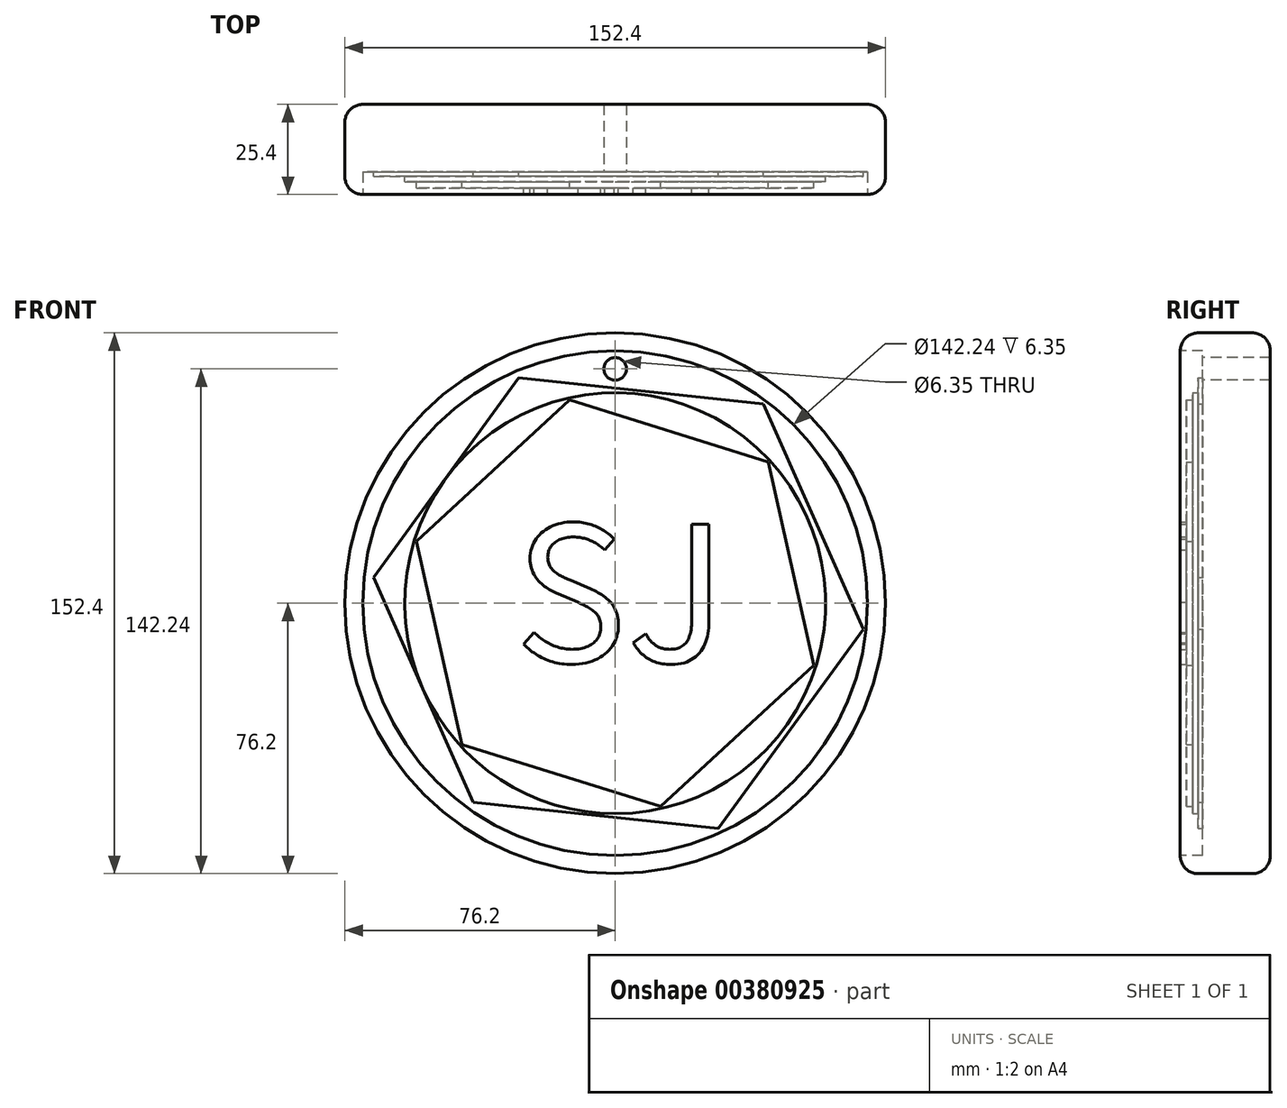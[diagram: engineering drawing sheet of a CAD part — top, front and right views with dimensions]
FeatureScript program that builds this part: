
annotation { "Feature Type Name" : "Feature", "Feature Type Description" : "" }
export const myFeature = defineFeature(function(context is Context, id is Id, definition is map)
    precondition{}
    {
        {
            var Q0;
            Q0=qCreatedBy(makeId("Front.planeOp"),FACE);
            var sketch = newSketch(context, id + "F0", { "sketchPlane" : qUnion([Q0])});
            skCircle(sketch, "E0", {"center": v(0, 0) * mm, "radius": 76.2 * mm});
            skSolve(sketch);
        }
        {
            var Q0;
            Q0 = qSketchRegion(id + "F0", true);
            extrude(context, id + "F1", {"entities" : qUnion([Q0]), "depth" : 25.4 * mm});
        }
        {
            var Q0;
            Q0=makeQuery(id+"F1.opExtrude","SWEPT_FACE",FACE,{"disambiguationData":[OSD([sQuery(id+"F0.wireOp",EDGE,"E0")])]});
            fillet(context, id + "F2", {"entities" : qUnion([Q0]), "radius" : 5.08 * mm, "tangentPropagation" : true, "allowEdgeOverflow" : false});
        }
        {
            var Q0;
            Q0=makeQuery(id+"F1.opExtrude","CAP_FACE",FACE,{"disambiguationData":[OSD([sQuery(id+"F0.wireOp",EDGE,"E0")])],"isStart":false});
            extrude(context, id + "F3", {"entities" : qUnion([Q0]), "operationType" : NewBodyOperationType.REMOVE, "oppositeDirection" : true, "depth" : 6.35 * mm});
        }
        {
            var Q0;
            Q0=makeQuery(id+"F3.boolean.opBoolean","COPY",FACE,{"derivedFrom":makeQuery(id+"F3.opExtrude","CAP_FACE",FACE,{"disambiguationData":[OSD([sQuery(id+"F0.wireOp",EDGE,"E0")])],"isStart":false})});
            var sketch = newSketch(context, id + "F4", { "sketchPlane" : qUnion([Q0])});
            skText(sketch, "E1", { "text": "SJ", "fontName": "NotoSansCJKjp-Regular.otf"});
            const initialGuessF4  = {"E1": [-0.02833, -0.01657, 1, 0, 0.0381]};
            skSetInitialGuess(sketch, initialGuessF4);
            skSolve(sketch);
        }
        {
            var Q0;
            Q0 = qSketchRegion(id + "F4", true);
            extrude(context, id + "F5", {"entities" : qUnion([Q0]), "operationType" : NewBodyOperationType.ADD, "depth" : 6.35 * mm});
        }
        {
            var Q0;
            Q0=makeQuery(id+"F3.boolean.opBoolean","COPY",FACE,{"derivedFrom":makeQuery(id+"F3.opExtrude","CAP_FACE",FACE,{"disambiguationData":[OSD([sQuery(id+"F0.wireOp",EDGE,"E0")])],"isStart":false})});
            var sketch = newSketch(context, id + "F6", { "sketchPlane" : qUnion([Q0])});
            skCircle(sketch, "E2", {"center": v(0, 66.04) * mm, "radius": 3.18 * mm});
            skSolve(sketch);
        }
        {
            var Q0;
            Q0=makeQuery(id+"F6.imprint","IMPRINT",FACE,{"disambiguationData":[TD([[makeQuery(id+"F6.imprint","IMPRINT",EDGE,{"derivedFrom":sQuery(id+"F6.wireOp",EDGE,"E2")}),1.0]])]});
            extrude(context, id + "F7", {"entities" : qUnion([Q0]), "operationType" : NewBodyOperationType.REMOVE, "oppositeDirection" : true, "depth" : 25.4 * mm});
        }
        {
            var Q0;
            Q0=makeQuery(id+"F3.boolean.opBoolean","COPY",FACE,{"derivedFrom":makeQuery(id+"F3.opExtrude","CAP_FACE",FACE,{"disambiguationData":[OSD([sQuery(id+"F0.wireOp",EDGE,"E0")])],"isStart":false})});
            var sketch = newSketch(context, id + "F8", { "sketchPlane" : qUnion([Q0])});
            skCircle(sketch, "E3.cCircle", {"center": v(0.93, 0) * mm, "radius": 60.15 * mm, "construction": true});
            skLineSegment(sketch, "E3.0", {"start": v(70, -7.34) * mm, "end": v(29.1, -63.49) * mm});
            skLineSegment(sketch, "E3.1", {"start": v(29.1, -63.49) * mm, "end": v(-39.97, -56.15) * mm});
            skLineSegment(sketch, "E3.2", {"start": v(-39.97, -56.15) * mm, "end": v(-68.14, 7.34) * mm});
            skLineSegment(sketch, "E3.3", {"start": v(-68.14, 7.34) * mm, "end": v(-27.25, 63.49) * mm});
            skLineSegment(sketch, "E3.4", {"start": v(-27.25, 63.49) * mm, "end": v(41.82, 56.15) * mm});
            skLineSegment(sketch, "E3.5", {"start": v(41.82, 56.15) * mm, "end": v(70, -7.34) * mm});
            skPoint(sketch, "E3.0.midPoint", {"position": v(49.55, -35.41) * mm});
            skSolve(sketch);
        }
        {
            var Q0;
            Q0 = qSketchRegion(id + "F8", true);
            extrude(context, id + "F9", {"entities" : qUnion([Q0]), "operationType" : NewBodyOperationType.ADD, "depth" : 1.27 * mm});
        }
        {
            var Q0;
            Q0=makeQuery(id+"F9.opExtrude","CAP_FACE",FACE,{"disambiguationData":[OSD([sQuery(id+"F8.wireOp",EDGE,"E3.0"),sQuery(id+"F8.wireOp",EDGE,"E3.1"),sQuery(id+"F8.wireOp",EDGE,"E3.2"),sQuery(id+"F8.wireOp",EDGE,"E3.3"),sQuery(id+"F8.wireOp",EDGE,"E3.4"),sQuery(id+"F8.wireOp",EDGE,"E3.5")])],"isStart":false});
            var sketch = newSketch(context, id + "F10", { "sketchPlane" : qUnion([Q0])});
            skCircle(sketch, "E4", {"center": v(0, 0) * mm, "radius": 59.3 * mm});
            skSolve(sketch);
        }
        {
            var Q0;
            Q0 = qSketchRegion(id + "F10", true);
            extrude(context, id + "F11", {"entities" : qUnion([Q0]), "operationType" : NewBodyOperationType.ADD, "depth" : 1.52 * mm});
        }
        {
            var Q0;
            Q0=makeQuery(id+"F11.opExtrude","CAP_FACE",FACE,{"disambiguationData":[OSD([sQuery(id+"F10.wireOp",EDGE,"E4")])],"isStart":false});
            var sketch = newSketch(context, id + "F12", { "sketchPlane" : qUnion([Q0])});
            skCircle(sketch, "E5.cCircle", {"center": v(0, 0) * mm, "radius": 50.84 * mm, "construction": true});
            skLineSegment(sketch, "E5.0", {"start": v(-12.86, 57.28) * mm, "end": v(43.18, 39.78) * mm});
            skLineSegment(sketch, "E5.1", {"start": v(43.18, 39.78) * mm, "end": v(56.04, -17.5) * mm});
            skLineSegment(sketch, "E5.2", {"start": v(56.04, -17.5) * mm, "end": v(12.86, -57.28) * mm});
            skLineSegment(sketch, "E5.3", {"start": v(12.86, -57.28) * mm, "end": v(-43.18, -39.78) * mm});
            skLineSegment(sketch, "E5.4", {"start": v(-43.18, -39.78) * mm, "end": v(-56.04, 17.5) * mm});
            skLineSegment(sketch, "E5.5", {"start": v(-56.04, 17.5) * mm, "end": v(-12.86, 57.28) * mm});
            skPoint(sketch, "E5.0.midPoint", {"position": v(15.16, 48.53) * mm});
            skSolve(sketch);
        }
        {
            var Q0;
            Q0 = qSketchRegion(id + "F12", true);
            extrude(context, id + "F13", {"entities" : qUnion([Q0]), "operationType" : NewBodyOperationType.ADD, "depth" : 1.78 * mm});
        }
    });
